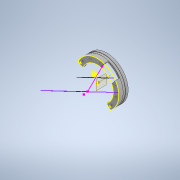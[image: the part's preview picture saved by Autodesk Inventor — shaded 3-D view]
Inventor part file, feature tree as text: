
AUTODESK INVENTOR PART (.ipt)
format: ipt  version: 2022 (Build 260153000, 153)  size: 307,200 bytes
history: native  units: in
note: dims shown in document units (in); Inventor stores cm internally (conversion verified against a paired STEP export)
features: other x10, reference x9, sketch x5, plane x3, extrude x2, projected_geometry x2, revolve x1, fillet x1, hole x1, pattern_circular x1
ambient origin geometry x8: Origin, YZ Plane, XZ Plane, XY Plane, X Axis, Y Axis, Z Axis, Center Point
bodies: Body1 (feature_tree)
feature tree (35):
  other  "Arbeitsachse1"
  plane  "Arbeitsebene4"
  revolve  "Umdrehung1"
  extrude  "Extrusion9"  Depth=0.1969in
  fillet  "Rundung2"  [1 undecoded]
  sketch  "Skizze13"  dims[d41=0.2362in]
  plane  "Arbeitsebene6"
  hole  "Bohrung1"  [1 undecoded]
  pattern_circular  "Runde Anordnung1"  Angle=360.0deg  [1 undecoded]
  sketch  "Skizze17"  dims[d43=0.0236in d44=360.0deg d46=0.3937in d47=0.0in d55=0.1969in d56=0.0118in d68=105.0deg d69=105.0deg d70=0.1102in d71=0.1102in d72=0.2362in d73=0.1969in d74=0.3937in d75=90.0deg d76=0.315in d77=0.8108in d78=4.7244in d79=360.0deg d81=0.1181in d82=0.3543in d83=0.0in]
  other  "Arbeitspunkt2"
  extrude  "Extrusion14"  Depth=0.1181in TaperAngle=0.0deg
  plane  "Arbeitsebene3"
  other  "Arbeitspunkt1"
  sketch  "Skizze10"  dims[d36=0.1575in d37=0.1969in d38=135.0deg]
  reference  "Referenz27"
  reference  "Referenz28"
  sketch  "Skizze11"  dims[d39=0.0118in d40=0.0984in]
  reference  "Referenz29"
  reference  "Referenz30"
  reference  "Referenz31"
  projected_geometry  "Projizierte Kontur8"
  projected_geometry  "Projizierte Kontur9"
  reference  "Referenz37"
  reference  "Referenz38"
  reference  "Referenz39"
  sketch  "Skizze16"  dims[d42=0.4724in]
  reference  "Referenz40"
  other  "Anglerfish_bonne_mamman_m12large_flipped_v0.iam"
  other  "00_Lid_Bonne_Mamman:1"
  other  "00_Coverglass:1"
  other  "Anglerfish_Lightplate_Tosslink:1"
  other  "Matchboxscope_M12_Lensadapter_v0:1"
  other  "00_toslink_launcher_v3:2"
  other  "00_toslink_launcher_v3:1"
note: 3 required parameter values undecoded (feature->parameter linkage not recoverable at this tier; creation-order binding heuristic only, values carry confidence <= 0.55)
